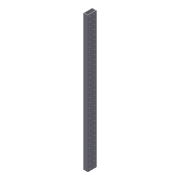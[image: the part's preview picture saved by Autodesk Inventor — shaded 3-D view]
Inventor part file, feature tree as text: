
AUTODESK INVENTOR PART (.ipt)
format: ipt  version: 2012 (Build 160160000, 160)  size: 188,416 bytes
history: native  units: in
note: dims shown in document units (in); Inventor stores cm internally (conversion verified against a paired STEP export)
features: extrude x2, sketch x2, shell x1, pattern_linear x1
ambient origin geometry x8: Origin, YZ Plane, XZ Plane, XY Plane, X Axis, Y Axis, Z Axis, Center Point
bodies: Solid1 (feature_tree)
feature tree (6):
  extrude  "Extrusion1"  Depth=2.0in
  shell  "Shell2"  Thickness=31.0in
  extrude  "Extrusion2"  Depth=0.1875in
  pattern_linear  "Rectangular Pattern1"  Spacing1=0.5in  [1 undecoded]
  sketch  "Sketch2"  dims[d0=1.0in d1=2.0in d2=31.0in d3=0.0in]
  sketch  "Sketch3"  dims[d5=0.125in d6=0.1875in d7=0.5in d8=0.5in d9=1.0in d10=0.0in d11=12.2047in d13=1.0in d14=0.7874in d16=1.0in]
note: 1 required parameter value undecoded (feature->parameter linkage not recoverable at this tier; creation-order binding heuristic only, values carry confidence <= 0.55)
